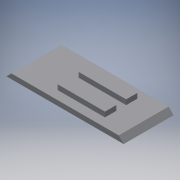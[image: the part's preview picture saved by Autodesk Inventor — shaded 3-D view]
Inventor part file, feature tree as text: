
AUTODESK INVENTOR PART (.ipt)
format: ipt  version: 2018.3 (Build 223284000, 284)  size: 111,616 bytes
history: native  units: mm
features: extrude x3, sketch x3
ambient origin geometry x8: Origin, YZ Plane, XZ Plane, XY Plane, X Axis, Y Axis, Z Axis, Center Point
bodies: Solid1 (feature_tree)
feature tree (6):
  extrude  "Extrusion1"  Depth=20.0mm
  extrude  "Extrusion2"  Depth=2.0mm
  extrude  "Extrusion5"  Depth=20.0mm TaperAngle=0.0deg
  sketch  "Sketch1"  dims[d0=43.0mm d1=20.0mm]
  sketch  "Sketch2"  dims[d2=2.0mm d3=0.0mm d4=2.0mm]
  sketch  "Sketch5"  dims[d5=2.0mm d6=20.0mm d7=0.0mm d39=2.0mm d40=0.0mm]
